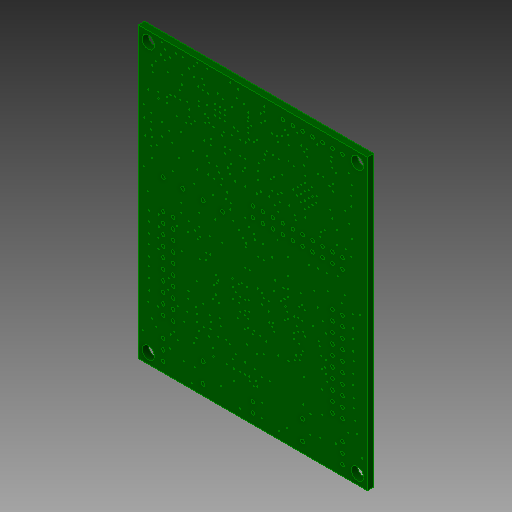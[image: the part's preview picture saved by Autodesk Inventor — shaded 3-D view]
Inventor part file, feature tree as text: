
AUTODESK INVENTOR PART (.ipt)
format: ipt  version: 2018 (Build 220112000, 112)  size: 889,856 bytes
history: native  units: in
note: dims shown in document units (in); Inventor stores cm internally (conversion verified against a paired STEP export)
features: other x1, sketch x1
ambient origin geometry x8: Origin, YZ Plane, XZ Plane, XY Plane, X Axis, Y Axis, Z Axis, Center Point
bodies: Solid1 (feature_tree)
feature tree (2):
  other  "MSP-EXP430F5529LP.brd_Outline"
  sketch  "Sketch1"  dims[d0=0.063in d1=0.0in]
